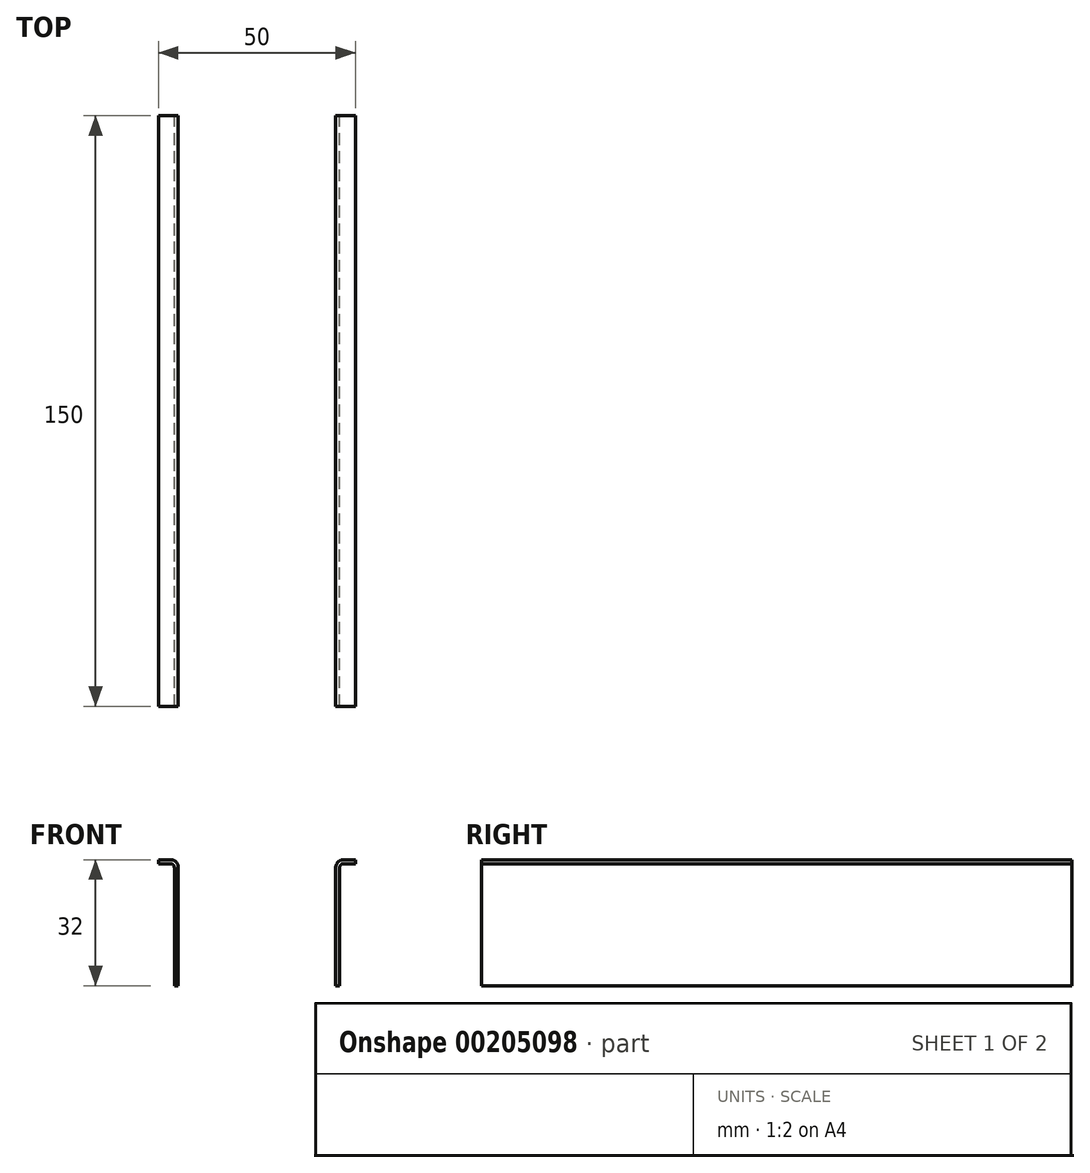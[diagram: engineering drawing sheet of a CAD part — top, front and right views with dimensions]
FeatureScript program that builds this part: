
annotation { "Feature Type Name" : "Feature", "Feature Type Description" : "" }
export const myFeature = defineFeature(function(context is Context, id is Id, definition is map)
    precondition{}
    {
        {
            var Q0;
            Q0=qCreatedBy(makeId("Front.planeOp"),FACE);
            var sketch = newSketch(context, id + "F0", { "sketchPlane" : qUnion([Q0])});
            skLineSegment(sketch, "E0", {"start": v(-25, 32) * mm, "end": v(-22, 32) * mm});
            skLineSegment(sketch, "E1", {"start": v(-20, 30) * mm, "end": v(-20, 0) * mm});
            skLineSegment(sketch, "E2", {"start": v(-20, 0) * mm, "end": v(-21, 0) * mm});
            skLineSegment(sketch, "E3", {"start": v(-21, 0) * mm, "end": v(-21, 30) * mm});
            skLineSegment(sketch, "E4", {"start": v(-25, 32) * mm, "end": v(-25, 31) * mm});
            skLineSegment(sketch, "E5", {"start": v(-25, 31) * mm, "end": v(-22, 31) * mm});
            skArc(sketch, "E6", {"start": v(-22, 32) * mm, "mid": v(-20.59, 31.41) * mm, "end": v(-20, 30) * mm});
            skArc(sketch, "E7", {"start": v(-22, 31) * mm, "mid": v(-21.3, 30.7) * mm, "end": v(-21, 30) * mm});
            skArc(sketch, "E8.MirrorCS", {"start": v(22, 31) * mm, "mid": v(21.3, 30.7) * mm, "end": v(21, 30) * mm});
            skLineSegment(sketch, "E9.MirrorCS", {"start": v(25, 31) * mm, "end": v(22, 31) * mm});
            skLineSegment(sketch, "E10.MirrorCS", {"start": v(25, 32) * mm, "end": v(25, 31) * mm});
            skLineSegment(sketch, "E11.MirrorCS", {"start": v(20, 0) * mm, "end": v(21, 0) * mm});
            skLineSegment(sketch, "E12.MirrorCS", {"start": v(25, 32) * mm, "end": v(22, 32) * mm});
            skArc(sketch, "E13.MirrorCS", {"start": v(22, 32) * mm, "mid": v(20.59, 31.41) * mm, "end": v(20, 30) * mm});
            skLineSegment(sketch, "E14.MirrorCS", {"start": v(20, 30) * mm, "end": v(20, 0) * mm});
            skLineSegment(sketch, "E15.MirrorCS", {"start": v(21, 0) * mm, "end": v(21, 30) * mm});
            skSolve(sketch);
        }
        {
            var Q0;
            Q0=makeQuery(id+"F0.imprint","IMPRINT",FACE,{"disambiguationData":[TD([[makeQuery(id+"F0.imprint","IMPRINT",EDGE,{"derivedFrom":sQuery(id+"F0.wireOp",EDGE,"E8.MirrorCS")}),-1.0]])]});
            var Q1;
            Q1=makeQuery(id+"F0.imprint","IMPRINT",FACE,{"disambiguationData":[TD([[makeQuery(id+"F0.imprint","IMPRINT",EDGE,{"derivedFrom":sQuery(id+"F0.wireOp",EDGE,"E0")}),-1.0]])]});
            extrude(context, id + "F1", {"entities" : qUnion([Q0, Q1]), "depth" : 150 * mm});
        }
    });
